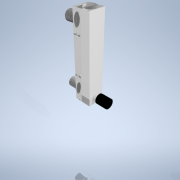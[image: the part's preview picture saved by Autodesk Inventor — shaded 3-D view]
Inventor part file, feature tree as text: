
AUTODESK INVENTOR PART (.ipt)
format: ipt  version: 2020 (Build 240168000, 168)  size: 287,744 bytes
history: native  units: mm
features: sketch x12, extrude x9, thread x6, fillet x2, plane x2, mirror x2, projected_geometry x1, other x1
ambient origin geometry x8: Origin, YZ Plane, XZ Plane, XY Plane, X Axis, Y Axis, Z Axis, Center Point
bodies: Solid1 (feature_tree)
feature tree (35):
  extrude  "Extrusion1"  Depth=34.9mm
  extrude  "Extrusion2"  Depth=6.0mm TaperAngle=0.0deg
  fillet  "Fillet1"  Radius=0.5mm
  sketch  "Sketch4"  dims[d13=85.25mm d14=90.0deg]
  plane  "Work Plane2"
  extrude  "Extrusion3"  TaperAngle=90.0deg  [1 undecoded]
  mirror  "Mirror1"
  extrude  "Extrusion4"  Depth=11.08mm
  extrude  "Extrusion5"  Depth=9.9mm
  sketch  "Sketch8"  dims[d37=19.7mm d38=0.0mm d39=19.7mm d40=0.0mm]
  plane  "Work Plane3"
  mirror  "Mirror2"
  thread  "Thread1"  [1 undecoded]
  thread  "Thread2"  [1 undecoded]
  thread  "Thread3"  [1 undecoded]
  thread  "Thread4"  [1 undecoded]
  thread  "Thread5"  [1 undecoded]
  thread  "Thread6"  [1 undecoded]
  extrude  "Extrusion6"  Depth=19.7mm TaperAngle=0.0deg
  fillet  "Fillet2"  Radius=19.7mm
  extrude  "Extrusion7"  Depth=19.7mm TaperAngle=0.0deg
  extrude  "Extrusion8"  Depth=4.0mm TaperAngle=0.0deg
  extrude  "Extrusion9"  Depth=1.0mm
  sketch  "Sketch13"  dims[d51=15.3mm d52=8.0mm d53=0.0mm d54=20.4mm d55=22.9mm d56=0.0mm]
  sketch  "Sketch1"  dims[d0=31.9mm d1=34.9mm]
  sketch  "Sketch2"  dims[d2=167.7mm d3=0.0mm d8=6.0mm d9=0.0mm d10=0.5mm]
  sketch  "Sketch5"  dims[d15=20.4mm d16=11.08mm]
  projected_geometry  "Projected Loop1"
  sketch  "Sketch6"  dims[d17=19.7mm d18=0.0mm d21=9.9mm d22=0.7mm d23=0.0mm d24=5.7mm d25=7.1mm d26=0.0mm d27=84.85mm d28=90.0deg d29=7.1mm d30=0.0mm]
  sketch  "Sketch7"  dims[d31=7.1mm d32=0.0mm d33=19.7mm d34=0.0mm d35=19.7mm d36=0.0mm]
  sketch  "Sketch9"  dims[d42=24.6mm d43=4.0mm d44=0.0mm]
  sketch  "Sketch10"  dims[d45=8.0mm d46=1.0mm]
  sketch  "Sketch11"  dims[d47=17.46mm]
  sketch  "Sketch12"  dims[d48=1.0mm d49=0.0mm]
  other  "Image1"
note: 7 required parameter values undecoded (feature->parameter linkage not recoverable at this tier; creation-order binding heuristic only, values carry confidence <= 0.55)
